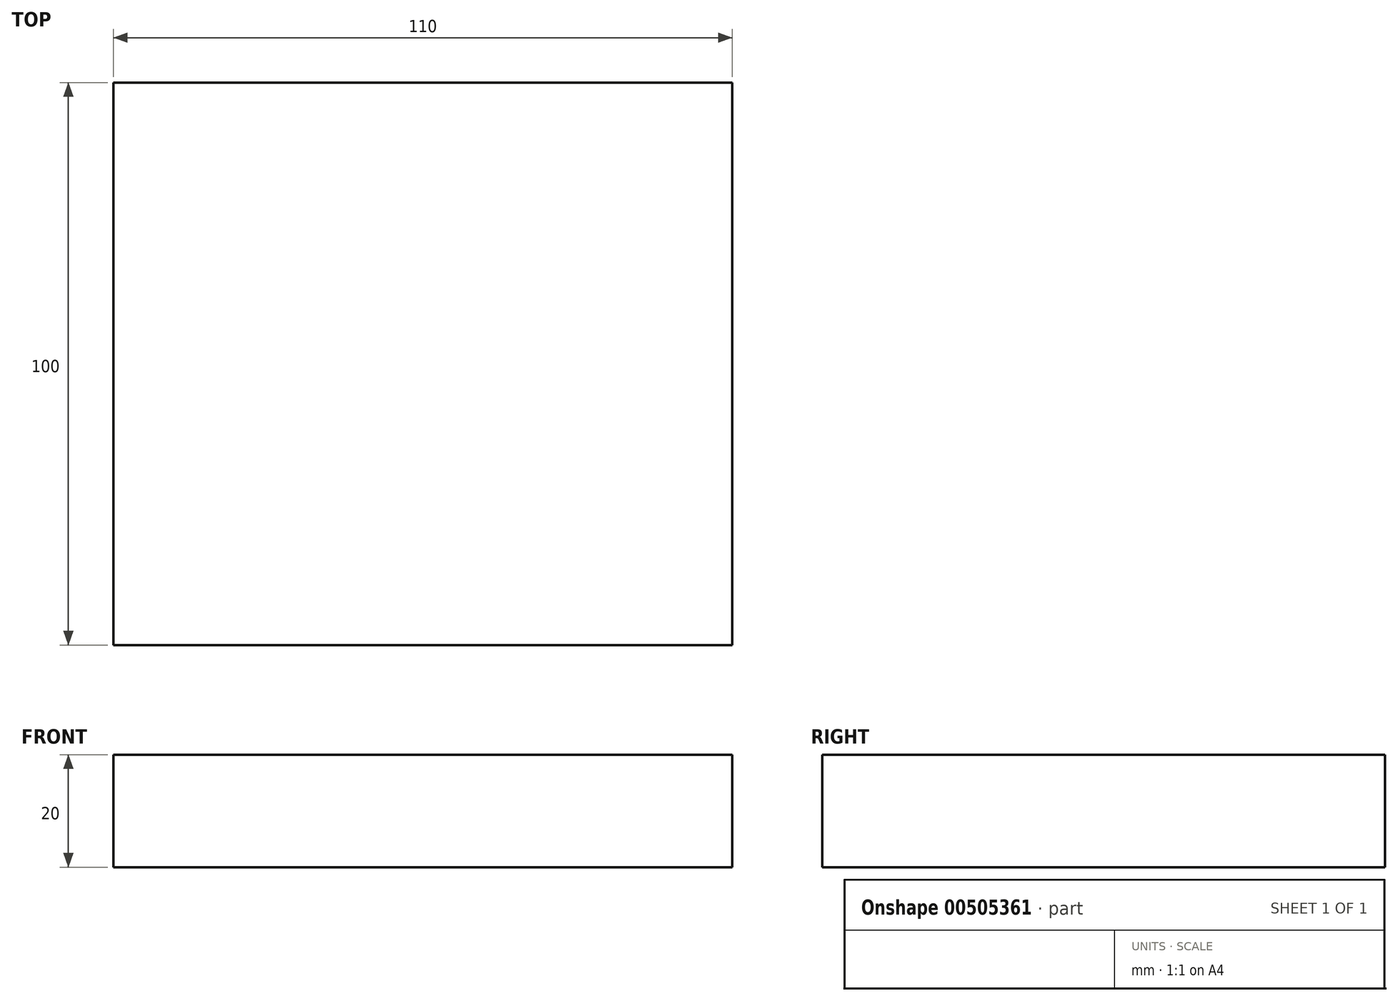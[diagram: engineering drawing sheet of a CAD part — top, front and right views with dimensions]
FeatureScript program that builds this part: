
annotation { "Feature Type Name" : "Feature", "Feature Type Description" : "" }
export const myFeature = defineFeature(function(context is Context, id is Id, definition is map)
    precondition{}
    {
        {
            var Q0;
            Q0=qCreatedBy(makeId("Top.planeOp"),FACE);
            var sketch = newSketch(context, id + "F0", { "sketchPlane" : qUnion([Q0])});
            skLineSegment(sketch, "E0.bottom", {"start": v(-83.47, 89.98) * mm, "end": v(26.53, 89.98) * mm});
            skLineSegment(sketch, "E0.top", {"start": v(-83.47, -10.02) * mm, "end": v(26.53, -10.02) * mm});
            skLineSegment(sketch, "E0.left", {"start": v(-83.47, 89.98) * mm, "end": v(-83.47, -10.02) * mm});
            skLineSegment(sketch, "E0.right", {"start": v(26.53, 89.98) * mm, "end": v(26.53, -10.02) * mm});
            skSolve(sketch);
        }
        {
            var Q0;
            Q0=makeQuery(id+"F0.imprint","IMPRINT",FACE,{"disambiguationData":[TD([[makeQuery(id+"F0.imprint","IMPRINT",EDGE,{"derivedFrom":sQuery(id+"F0.wireOp",EDGE,"E0.bottom")}),-1.0]])]});
            extrude(context, id + "F1", {"entities" : qUnion([Q0]), "depth" : 20 * mm});
        }
    });
